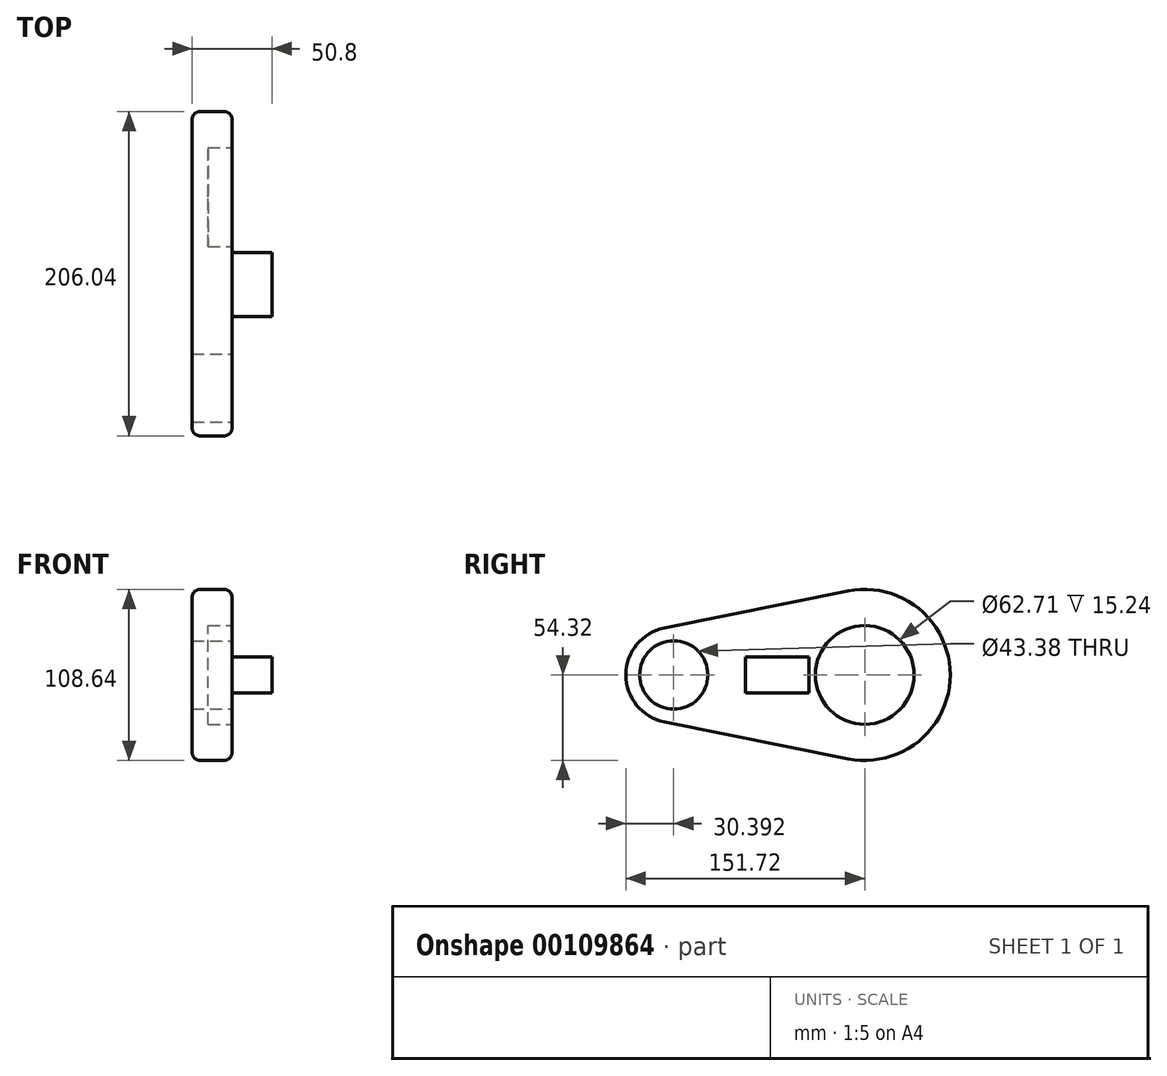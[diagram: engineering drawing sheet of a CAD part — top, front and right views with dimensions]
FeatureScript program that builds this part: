
annotation { "Feature Type Name" : "Feature", "Feature Type Description" : "" }
export const myFeature = defineFeature(function(context is Context, id is Id, definition is map)
    precondition{}
    {
        {
            var Q0;
            Q0=qCreatedBy(makeId("Right.planeOp"),FACE);
            var sketch = newSketch(context, id + "F0", { "sketchPlane" : qUnion([Q0])});
            skCircle(sketch, "E0", {"center": v(-42, 0) * mm, "radius": 30.39 * mm});
            skCircle(sketch, "E1", {"center": v(79.33, 0) * mm, "radius": 54.32 * mm});
            skLineSegment(sketch, "E2", {"start": v(-48, 29.8) * mm, "end": v(68.62, 53.25) * mm});
            skLineSegment(sketch, "E3", {"start": v(-48, -29.8) * mm, "end": v(68.62, -53.25) * mm});
            skSolve(sketch);
        }
        {
            var Q0;
            {var subQ0=sQuery(id+"F0.wireOp",EDGE,"E1");var subQ1=makeQuery(id+"F0.imprint","INTERSECT",VERTEX,{"derivedFrom":[subQ0,sQuery(id+"F0.wireOp",EDGE,"E2")]});Q0=makeQuery(id+"F0.imprint","IMPRINT",FACE,{"disambiguationData":[TD([[makeQuery(id+"F0.imprint","IMPRINT",EDGE,{"disambiguationData":[TD([[subQ1,-1.0]])],"derivedFrom":subQ0}),1.0]])]});}
            var Q1;
            {var subQ0=sQuery(id+"F0.wireOp",EDGE,"E0");var subQ1=makeQuery(id+"F0.imprint","INTERSECT",VERTEX,{"derivedFrom":[subQ0,sQuery(id+"F0.wireOp",EDGE,"E2")]});Q1=makeQuery(id+"F0.imprint","IMPRINT",FACE,{"disambiguationData":[TD([[makeQuery(id+"F0.imprint","IMPRINT",EDGE,{"disambiguationData":[TD([[subQ1,-1.0]])],"derivedFrom":subQ0}),1.0]])]});}
            var Q2;
            {var subQ0=sQuery(id+"F0.wireOp",EDGE,"E2");Q2=makeQuery(id+"F0.imprint","IMPRINT",FACE,{"disambiguationData":[TD([[makeQuery(id+"F0.imprint","IMPRINT",EDGE,{"derivedFrom":subQ0}),-1.0]])]});}
            extrude(context, id + "F1", {"entities" : qUnion([Q0, Q1, Q2]), "depth" : 25.4 * mm});
        }
        {
            var Q0;
            Q0=makeQuery(id+"F1.opExtrude","CAP_FACE",FACE,{"disambiguationData":[OSD([sQuery(id+"F0.wireOp",EDGE,"E0"),sQuery(id+"F0.wireOp",EDGE,"E1"),sQuery(id+"F0.wireOp",EDGE,"E2"),sQuery(id+"F0.wireOp",EDGE,"E3")])],"isStart":false});
            var sketch = newSketch(context, id + "F2", { "sketchPlane" : qUnion([Q0])});
            skCircle(sketch, "E4", {"center": v(79.33, 0) * mm, "radius": 31.35 * mm});
            skSolve(sketch);
        }
        {
            var Q0;
            Q0=makeQuery(id+"F2.imprint","IMPRINT",FACE,{"disambiguationData":[TD([[makeQuery(id+"F2.imprint","IMPRINT",EDGE,{"derivedFrom":sQuery(id+"F2.wireOp",EDGE,"E4")}),-1.0]])]});
            var sketch = newSketch(context, id + "F3", { "sketchPlane" : qUnion([Q0])});
            skCircle(sketch, "E5", {"center": v(-38.83, 0) * mm, "radius": 18.84 * mm});
            skLineSegment(sketch, "E6.bottom", {"start": v(3.45, 11.35) * mm, "end": v(43.95, 11.35) * mm});
            skLineSegment(sketch, "E6.top", {"start": v(3.45, -11.35) * mm, "end": v(43.95, -11.35) * mm});
            skLineSegment(sketch, "E6.left", {"start": v(3.45, 11.35) * mm, "end": v(3.45, -11.35) * mm});
            skLineSegment(sketch, "E6.right", {"start": v(43.95, 11.35) * mm, "end": v(43.95, -11.35) * mm});
            skPoint(sketch, "E6.middle", {"position": v(23.7, 0) * mm});
            skSolve(sketch);
        }
        {
            var Q0;
            Q0=makeQuery(id+"F3.imprint","IMPRINT",FACE,{"disambiguationData":[TD([[makeQuery(id+"F3.imprint","IMPRINT",EDGE,{"derivedFrom":sQuery(id+"F3.wireOp",EDGE,"E6.bottom")}),-1.0]])]});
            extrude(context, id + "F4", {"entities" : qUnion([Q0]), "operationType" : NewBodyOperationType.ADD, "depth" : 25.4 * mm});
        }
        {
            var Q0;
            Q0=makeQuery(id+"F2.imprint","IMPRINT",FACE,{"disambiguationData":[TD([[makeQuery(id+"F2.imprint","IMPRINT",EDGE,{"derivedFrom":sQuery(id+"F2.wireOp",EDGE,"E4")}),1.0]])]});
            extrude(context, id + "F5", {"entities" : qUnion([Q0]), "operationType" : NewBodyOperationType.REMOVE, "oppositeDirection" : true, "depth" : 15.24 * mm});
        }
        {
            var Q0;
            Q0=makeQuery(id+"F1.opExtrude","CAP_FACE",FACE,{"disambiguationData":[OSD([sQuery(id+"F0.wireOp",EDGE,"E0"),sQuery(id+"F0.wireOp",EDGE,"E1"),sQuery(id+"F0.wireOp",EDGE,"E2"),sQuery(id+"F0.wireOp",EDGE,"E3")])],"isStart":false});
            var sketch = newSketch(context, id + "F6", { "sketchPlane" : qUnion([Q0])});
            skCircle(sketch, "E7", {"center": v(-42, 0) * mm, "radius": 21.69 * mm});
            skSolve(sketch);
        }
        {
            var Q0;
            Q0=makeQuery(id+"F6.imprint","IMPRINT",FACE,{"disambiguationData":[TD([[makeQuery(id+"F6.imprint","IMPRINT",EDGE,{"derivedFrom":sQuery(id+"F6.wireOp",EDGE,"E7")}),1.0]])]});
            extrude(context, id + "F7", {"entities" : qUnion([Q0]), "operationType" : NewBodyOperationType.REMOVE, "oppositeDirection" : true, "depth" : 25.4 * mm});
        }
        {
            var Q0;
            Q0=makeQuery(id+"F1.opExtrude","SWEPT_FACE",FACE,{"disambiguationData":[OSD([sQuery(id+"F0.wireOp",EDGE,"E0")])]});
            fillet(context, id + "F8", {"entities" : qUnion([Q0]), "radius" : 5.08 * mm, "tangentPropagation" : true, "allowEdgeOverflow" : false});
        }
    });
